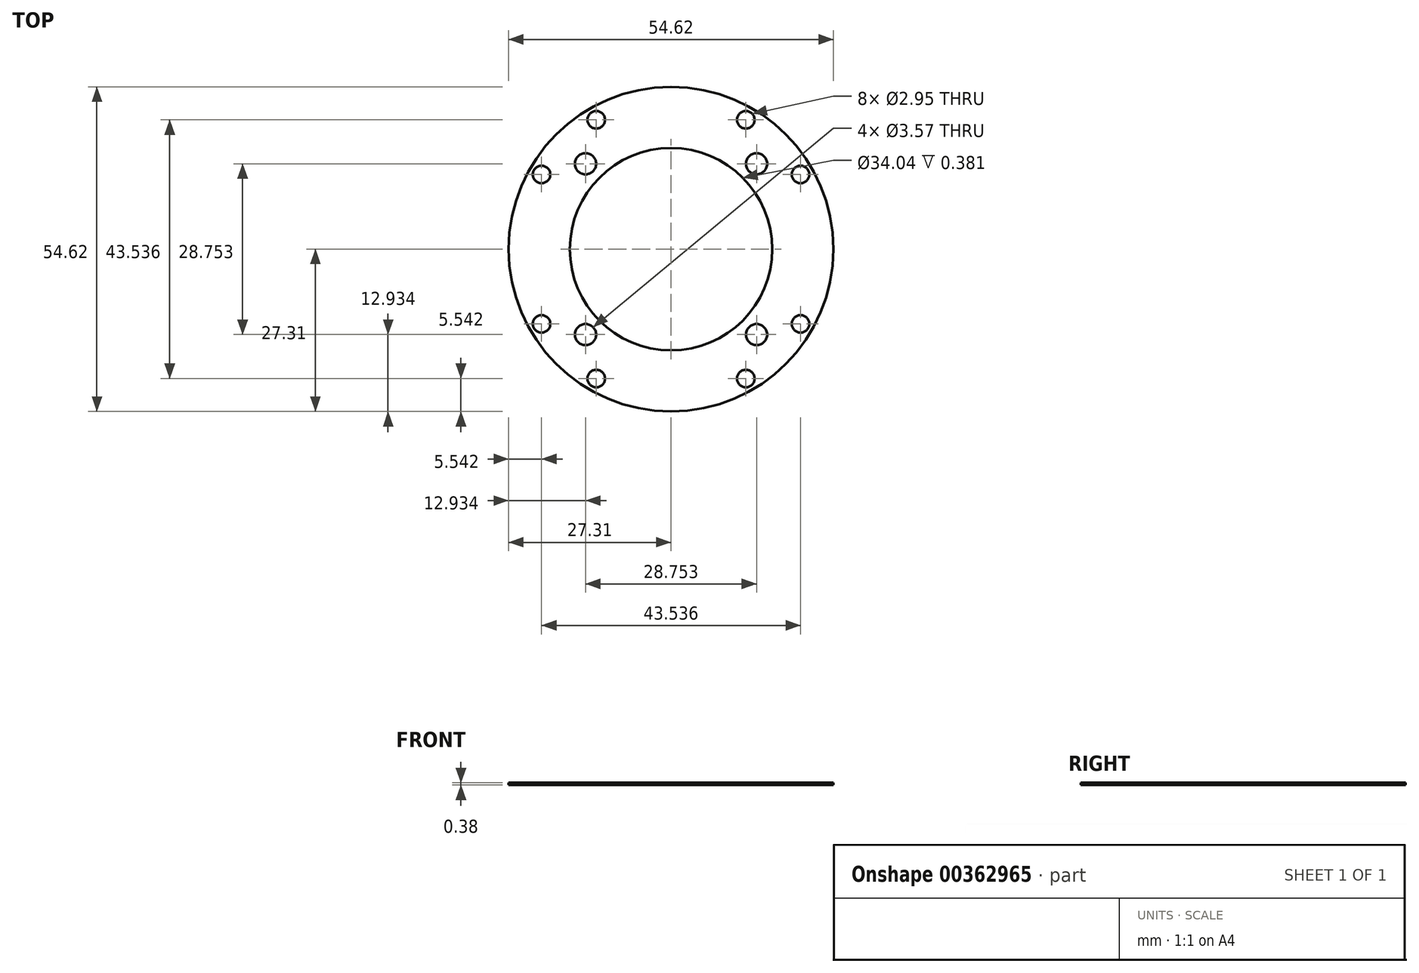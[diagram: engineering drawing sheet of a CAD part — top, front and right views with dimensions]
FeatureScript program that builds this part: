
annotation { "Feature Type Name" : "Feature", "Feature Type Description" : "" }
export const myFeature = defineFeature(function(context is Context, id is Id, definition is map)
    precondition{}
    {
        {
            var Q0;
            Q0=qCreatedBy(makeId("Top.planeOp"),FACE);
            var sketch = newSketch(context, id + "F0", { "sketchPlane" : qUnion([Q0])});
            skCircle(sketch, "E0", {"center": v(0, 0) * mm, "radius": 27.3 * mm});
            skCircle(sketch, "E1", {"center": v(0, 0) * mm, "radius": 17.02 * mm});
            skPoint(sketch, "E2", {"position": v(12.57, 21.77) * mm});
            skPoint(sketch, "E3", {"position": v(21.77, 12.57) * mm});
            skPoint(sketch, "E4", {"position": v(14.38, 14.38) * mm});
            skPoint(sketch, "E5.1.0", {"position": v(-21.77, 12.57) * mm});
            skPoint(sketch, "E5.1.2", {"position": v(-12.57, 21.77) * mm});
            skPoint(sketch, "E5.1.3", {"position": v(-14.38, 14.38) * mm});
            skPoint(sketch, "E5.2.0", {"position": v(-12.57, -21.77) * mm});
            skPoint(sketch, "E5.2.2", {"position": v(-21.77, -12.57) * mm});
            skPoint(sketch, "E5.2.3", {"position": v(-14.38, -14.38) * mm});
            skPoint(sketch, "E5.3.0", {"position": v(21.77, -12.57) * mm});
            skPoint(sketch, "E5.3.2", {"position": v(12.57, -21.77) * mm});
            skPoint(sketch, "E5.3.3", {"position": v(14.38, -14.38) * mm});
            skSolve(sketch);
        }
        {
            var Q0;
            Q0=makeQuery(id+"F0.imprint","IMPRINT",FACE,{"disambiguationData":[TD([[makeQuery(id+"F0.imprint","IMPRINT",EDGE,{"derivedFrom":sQuery(id+"F0.wireOp",EDGE,"E1")}),-1.0]])]});
            extrude(context, id + "F1", {"entities" : qUnion([Q0]), "oppositeDirection" : true, "depth" : 0.38 * mm});
        }
        {
            var Q0;
            Q0=sQuery(id+"F0.wireOp",VERTEX,"E2");
            var Q1;
            Q1=sQuery(id+"F0.wireOp",VERTEX,"E3");
            var Q2;
            Q2=sQuery(id+"F0.wireOp",VERTEX,"E5.3.0");
            var Q3;
            Q3=sQuery(id+"F0.wireOp",VERTEX,"E5.3.2");
            var Q4;
            Q4=sQuery(id+"F0.wireOp",VERTEX,"E5.2.0");
            var Q5;
            Q5=sQuery(id+"F0.wireOp",VERTEX,"E5.2.2");
            var Q6;
            Q6=sQuery(id+"F0.wireOp",VERTEX,"E5.1.0");
            var Q7;
            Q7=sQuery(id+"F0.wireOp",VERTEX,"E5.1.2");
            var Q8;
            Q8=makeQuery(id+"F1.opExtrude","SWEPT_BODY",BODY,{"disambiguationData":[OSD([sQuery(id+"F0.wireOp",EDGE,"E1"),sQuery(id+"F0.wireOp",EDGE,"E0")])]});
            hole(context, id + "F2", {"style" : HoleStyle.SIMPLE, "endStyle" : HoleEndStyle.THROUGH, "standardTappedOrClearance" : lookupTablePath({ "standard" : "ANSI", "size" : "#32 (0.12)", "type" : "Drilled" }), "standardBlindInLast" : lookupTablePath({ "standard" : "ANSI", "size" : "#32", "type" : "Drilled" }), "holeDiameter" : 2.95 * mm, "isTappedThrough" : true, "tappedDepth" : 4.57 * mm, "tapClearance" : 3, "startFromSketch" : true, "locations" : qUnion([Q0, Q1, Q2, Q3, Q4, Q5, Q6, Q7]), "scope" : qUnion([Q8])});
        }
        {
            var Q0;
            Q0=sQuery(id+"F0.wireOp",VERTEX,"E4");
            var Q1;
            Q1=sQuery(id+"F0.wireOp",VERTEX,"E5.3.3");
            var Q2;
            Q2=sQuery(id+"F0.wireOp",VERTEX,"E5.2.3");
            var Q3;
            Q3=sQuery(id+"F0.wireOp",VERTEX,"E5.1.3");
            var Q4;
            Q4=makeQuery(id+"F1.opExtrude","SWEPT_BODY",BODY,{"disambiguationData":[OSD([sQuery(id+"F0.wireOp",EDGE,"E1"),sQuery(id+"F0.wireOp",EDGE,"E0")])]});
            hole(context, id + "F3", {"style" : HoleStyle.SIMPLE, "endStyle" : HoleEndStyle.THROUGH, "standardTappedOrClearance" : lookupTablePath({ "standard" : "ANSI", "size" : "#28 (0.14)", "type" : "Drilled" }), "standardBlindInLast" : lookupTablePath({ "standard" : "ANSI", "size" : "#28", "type" : "Drilled" }), "holeDiameter" : 3.57 * mm, "isTappedThrough" : true, "tappedDepth" : 4.57 * mm, "tapClearance" : 3, "startFromSketch" : true, "locations" : qUnion([Q0, Q1, Q2, Q3]), "scope" : qUnion([Q4])});
        }
    });
